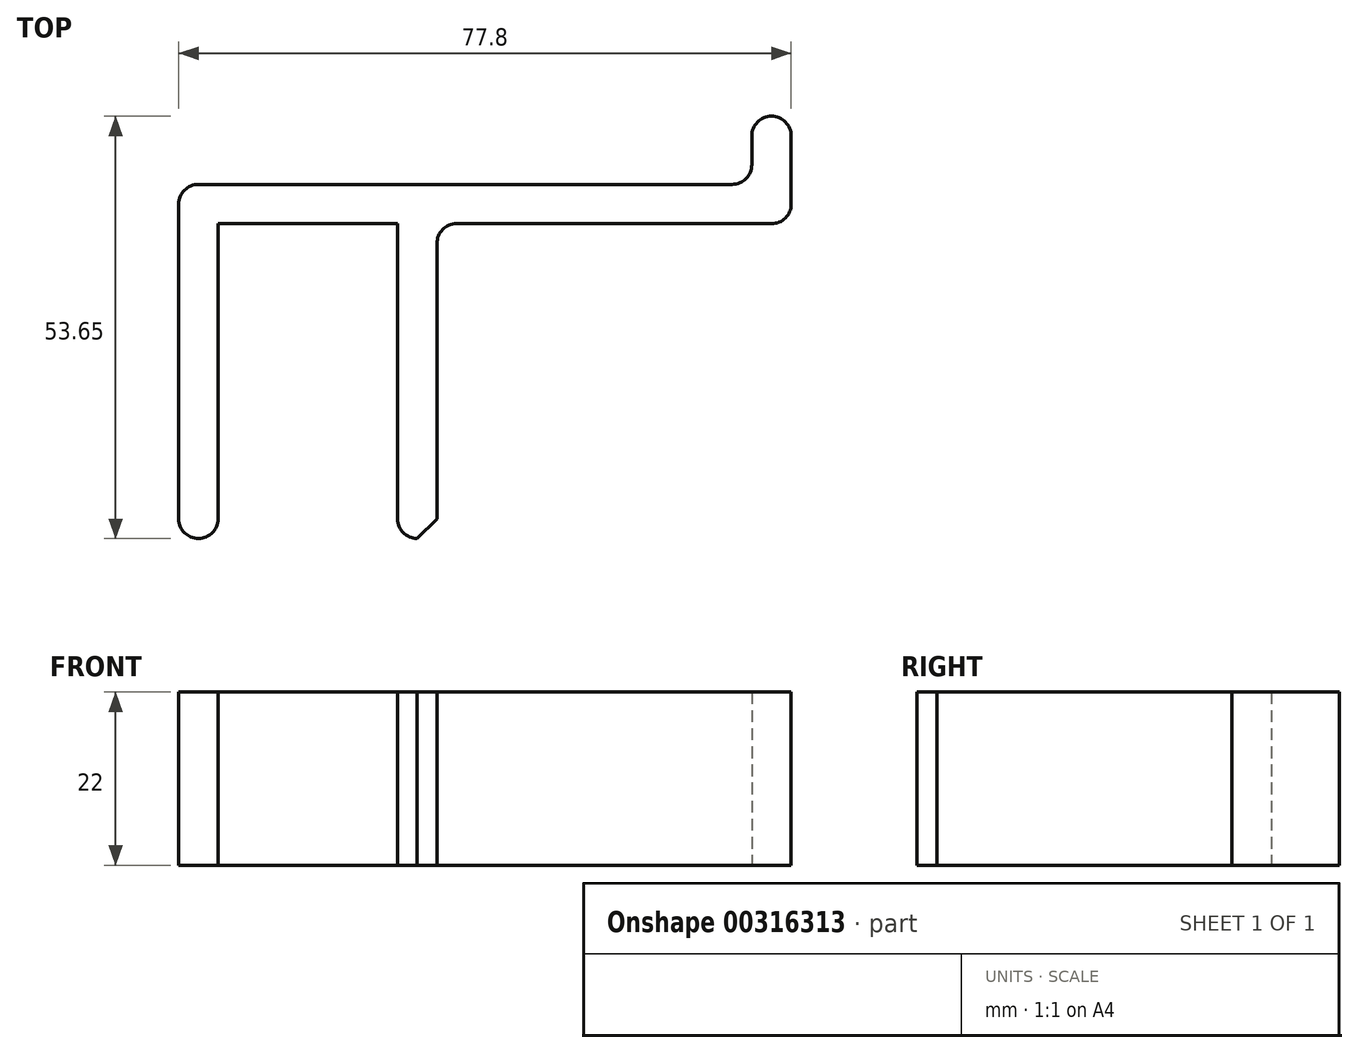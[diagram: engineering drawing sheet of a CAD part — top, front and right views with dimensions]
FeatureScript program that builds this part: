
annotation { "Feature Type Name" : "Feature", "Feature Type Description" : "" }
export const myFeature = defineFeature(function(context is Context, id is Id, definition is map)
    precondition{}
    {
        {
            var Q0;
            Q0=qCreatedBy(makeId("Top.planeOp"),FACE);
            var sketch = newSketch(context, id + "F0", { "sketchPlane" : qUnion([Q0])});
            skLineSegment(sketch, "E0", {"start": v(0, 0) * mm, "end": v(22.8, 0) * mm});
            skLineSegment(sketch, "E1", {"start": v(22.8, 0) * mm, "end": v(22.8, -40) * mm});
            skLineSegment(sketch, "E2", {"start": v(22.8, -40) * mm, "end": v(22.8, -40) * mm});
            skLineSegment(sketch, "E3", {"start": v(22.8, -40) * mm, "end": v(27.8, -40) * mm});
            skLineSegment(sketch, "E4", {"start": v(27.8, -40) * mm, "end": v(27.8, 0) * mm});
            skLineSegment(sketch, "E5", {"start": v(27.8, 0) * mm, "end": v(72.8, 0) * mm});
            skLineSegment(sketch, "E6", {"start": v(72.8, 0) * mm, "end": v(72.8, 13.65) * mm});
            skLineSegment(sketch, "E7", {"start": v(72.8, 13.65) * mm, "end": v(67.8, 13.65) * mm});
            skLineSegment(sketch, "E8", {"start": v(67.8, 13.65) * mm, "end": v(67.8, 5) * mm});
            skLineSegment(sketch, "E9", {"start": v(67.8, 5) * mm, "end": v(-5, 5) * mm});
            skLineSegment(sketch, "E10", {"start": v(-5, 5) * mm, "end": v(-5, -40) * mm});
            skLineSegment(sketch, "E11", {"start": v(-5, -40) * mm, "end": v(0, -40) * mm});
            skLineSegment(sketch, "E12", {"start": v(0, -40) * mm, "end": v(0, 0) * mm});
            skSolve(sketch);
        }
        {
            var Q0;
            Q0 = qSketchRegion(id + "F0", true);
            extrude(context, id + "F1", {"entities" : qUnion([Q0]), "depth" : 22 * mm});
        }
        {
            var Q0;
            Q0=makeQuery(id+"F1.opExtrude","SWEPT_EDGE",EDGE,{"disambiguationData":[OSD([sQuery(id+"F0.wireOp",EDGE,"E5"),sQuery(id+"F0.wireOp",EDGE,"E6")])]});
            var Q1;
            Q1=makeQuery(id+"F1.opExtrude","SWEPT_EDGE",EDGE,{"disambiguationData":[OSD([sQuery(id+"F0.wireOp",EDGE,"E4"),sQuery(id+"F0.wireOp",EDGE,"E5")])]});
            var Q2;
            Q2=makeQuery(id+"F1.opExtrude","SWEPT_EDGE",EDGE,{"disambiguationData":[OSD([sQuery(id+"F0.wireOp",EDGE,"E8"),sQuery(id+"F0.wireOp",EDGE,"E9")])]});
            var Q3;
            Q3=makeQuery(id+"F1.opExtrude","SWEPT_EDGE",EDGE,{"disambiguationData":[OSD([sQuery(id+"F0.wireOp",EDGE,"E7"),sQuery(id+"F0.wireOp",EDGE,"E8")])]});
            var Q4;
            Q4=makeQuery(id+"F1.opExtrude","SWEPT_EDGE",EDGE,{"disambiguationData":[OSD([sQuery(id+"F0.wireOp",EDGE,"E6"),sQuery(id+"F0.wireOp",EDGE,"E7")])]});
            var Q5;
            Q5=makeQuery(id+"F1.opExtrude","SWEPT_EDGE",EDGE,{"disambiguationData":[OSD([sQuery(id+"F0.wireOp",EDGE,"E9"),sQuery(id+"F0.wireOp",EDGE,"E10")])]});
            var Q6;
            Q6=makeQuery(id+"F1.opExtrude","SWEPT_EDGE",EDGE,{"disambiguationData":[OSD([sQuery(id+"F0.wireOp",EDGE,"E10"),sQuery(id+"F0.wireOp",EDGE,"E11")])]});
            var Q7;
            Q7=makeQuery(id+"F1.opExtrude","SWEPT_EDGE",EDGE,{"disambiguationData":[OSD([sQuery(id+"F0.wireOp",EDGE,"E11"),sQuery(id+"F0.wireOp",EDGE,"E12")])]});
            fillet(context, id + "F2", {"entities" : qUnion([Q0, Q1, Q2, Q3, Q4, Q5, Q6, Q7]), "radius" : 2.5 * mm, "tangentPropagation" : true, "allowEdgeOverflow" : false});
        }
        {
            var Q0;
            Q0=makeQuery(id+"F1.opExtrude","SWEPT_EDGE",EDGE,{"disambiguationData":[OSD([sQuery(id+"F0.wireOp",EDGE,"E3"),sQuery(id+"F0.wireOp",EDGE,"E4")])]});
            chamfer(context, id + "F3", {"entities" : qUnion([Q0]), "width" : 2.5 * mm, "tangentPropagation" : true});
        }
        {
            var Q0;
            Q0=makeQuery(id+"F1.opExtrude","SWEPT_EDGE",EDGE,{"disambiguationData":[OSD([sQuery(id+"F0.wireOp",EDGE,"E1"),sQuery(id+"F0.wireOp",EDGE,"E3")])]});
            fillet(context, id + "F4", {"entities" : qUnion([Q0]), "radius" : 2.5 * mm, "tangentPropagation" : true, "allowEdgeOverflow" : false});
        }
    });
